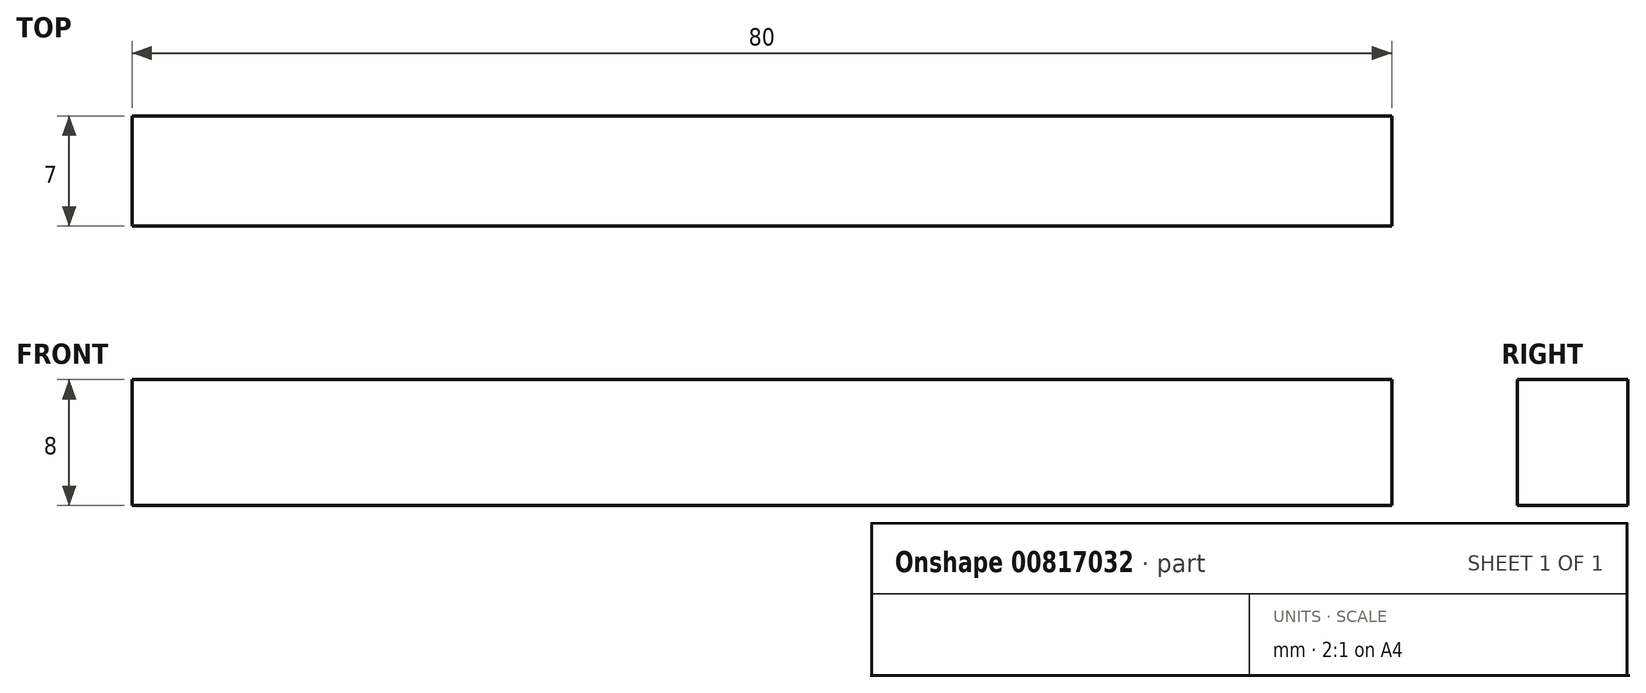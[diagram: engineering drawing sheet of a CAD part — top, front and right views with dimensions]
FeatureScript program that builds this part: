
annotation { "Feature Type Name" : "Feature", "Feature Type Description" : "" }
export const myFeature = defineFeature(function(context is Context, id is Id, definition is map)
    precondition{}
    {
        {
            var Q0;
            Q0=qCreatedBy(makeId("Front.planeOp"),FACE);
            var sketch = newSketch(context, id + "F0", { "sketchPlane" : qUnion([Q0])});
            skLineSegment(sketch, "E0.bottom", {"start": v(-40, 4) * mm, "end": v(40, 4) * mm});
            skLineSegment(sketch, "E0.top", {"start": v(-40, -4) * mm, "end": v(40, -4) * mm});
            skLineSegment(sketch, "E0.left", {"start": v(-40, 4) * mm, "end": v(-40, -4) * mm});
            skLineSegment(sketch, "E0.right", {"start": v(40, 4) * mm, "end": v(40, -4) * mm});
            skPoint(sketch, "E0.middle", {"position": v(0, 0) * mm});
            skSolve(sketch);
        }
        {
            var Q0;
            Q0=makeQuery(id+"F0.imprint","IMPRINT",FACE,{"disambiguationData":[TD([[makeQuery(id+"F0.imprint","IMPRINT",EDGE,{"derivedFrom":sQuery(id+"F0.wireOp",EDGE,"E0.bottom")}),-1.0]])]});
            extrude(context, id + "F1", {"entities" : qUnion([Q0]), "depth" : 7 * mm, "offsetDistance" : 25 * mm});
        }
    });
